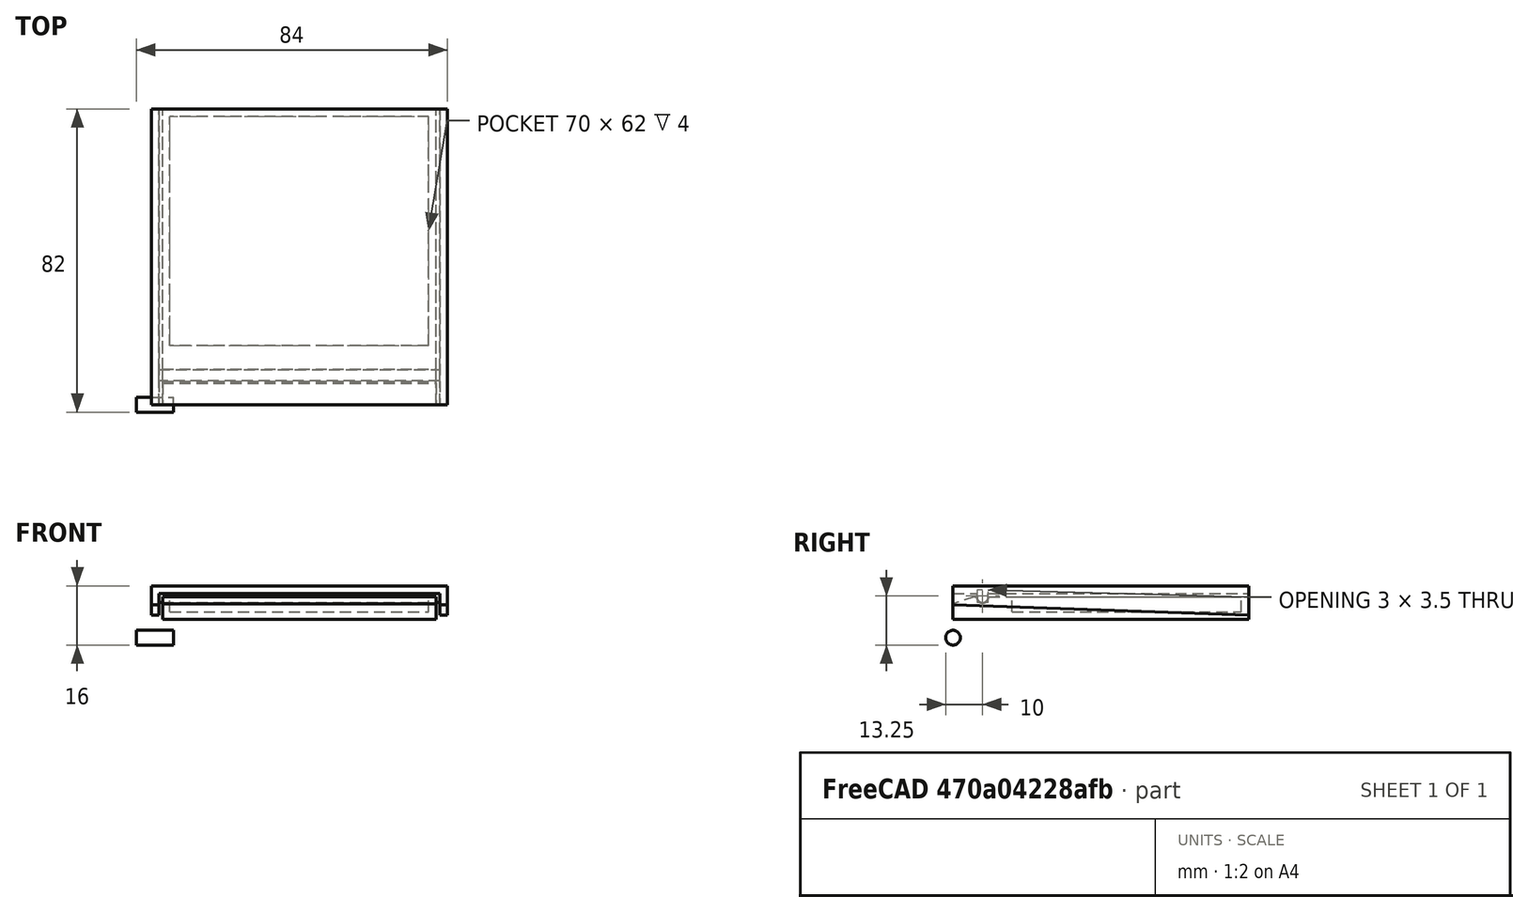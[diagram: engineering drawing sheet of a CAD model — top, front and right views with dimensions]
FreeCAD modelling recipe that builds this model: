
FCSTD DOCUMENT  (FreeCAD 0.16R6712 (Git))
Label: inclined
License: All rights reserved
LicenseURL: http://en.wikipedia.org/wiki/All_rights_reserved
objects: Part::Box×7, Part::Cut×5, Part::Cylinder×3, Part::Fuse×2
note: 17 computed .brp shape members not serialized (recipe doc carries the construction recipe); baked Part::Feature solids carry a one-line shape summary decoded from their .brp

FEATURE [Part::Box] Box  label="Cube"
  Height = 8
  Length = 80
  Placement = pos=(0,0,6) rot=(0,0,1;0rad)
  Width = 80
FEATURE [Part::Box] Box001  label="Cube001"
  Height = 12
  Length = 76
  Placement = pos=(2,0,0) rot=(0,0,1;0rad)
  Width = 80
FEATURE [Part::Cut] Cut
  Base = -> Box
  Tool = -> Box001
FEATURE [Part::Box] Box002  label="Cube002"
  Height = 3
  Length = 84
  Placement = pos=(-2,-2,6) rot=(-1,0,0;0.034907rad)
  Width = 84
FEATURE [Part::Cut] Cut001
  Base = -> Cut
  Tool = -> Box002
FEATURE [Part::Cylinder] Cylinder
  Angle = 360
  Height = 80
  Placement = pos=(0,3,11) rot=(0,1,0;1.5708rad)
  Radius = 1.5
  expr: Height = 80
FEATURE [Part::Box] Box003  label="Cube003"
  Height = 6
  Length = 74
  Placement = pos=(3,0,5) rot=(0,0,1;0rad)
  Width = 80
FEATURE [Part::Cylinder] Cylinder002
  Angle = 360
  Height = 10
  Placement = pos=(-4,0,0) rot=(0,1,0;1.5708rad)
  Radius = 2
FEATURE [Part::Cylinder] Cylinder003
  Angle = 360
  Height = 88
  Placement = pos=(-4,8,11) rot=(0,1,0;1.5708rad)
  Radius = 1.65
FEATURE [Part::Box] Box004  label="Cube004"
  Height = 2
  Length = 80
  Placement = pos=(0,1.5,11) rot=(0,0,1;0rad)
  Width = 3
FEATURE [Part::Fuse] Fusion
  Base = -> Cylinder
  Placement = pos=(0,5,0) rot=(0,0,1;0rad)
  Tool = -> Box004
FEATURE [Part::Fuse] Fusion001  label="top"
  Base = -> Cut001
  Tool = -> Fusion
FEATURE [Part::Box] Box005  label="Cube005"
  Height = 6
  Length = 70
  Placement = pos=(5,16,7) rot=(0,0,1;0rad)
  Width = 62
FEATURE [Part::Cut] Cut002
  Base = -> Box003
  Tool = -> Box005
FEATURE [Part::Cut] Cut003
  Base = -> Cut002
  Tool = -> Cylinder003
FEATURE [Part::Box] Box006  label="Cube006"
  Height = 10
  Length = 90
  Placement = pos=(0,-0.5,9) rot=(1,0,0;0.305433rad)
  Width = 10
FEATURE [Part::Cut] Cut004  label="bottom"
  Base = -> Cut003
  Tool = -> Box006
